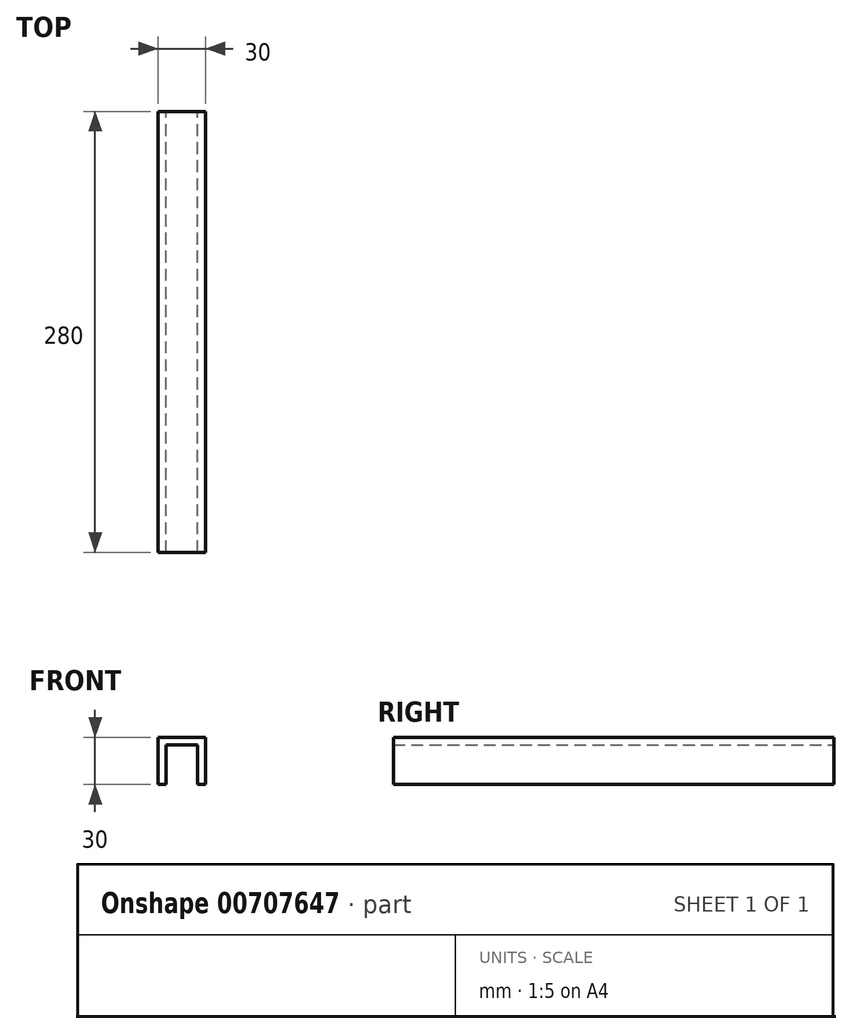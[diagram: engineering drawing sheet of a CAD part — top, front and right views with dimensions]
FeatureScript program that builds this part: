
annotation { "Feature Type Name" : "Feature", "Feature Type Description" : "" }
export const myFeature = defineFeature(function(context is Context, id is Id, definition is map)
    precondition{}
    {
        {
            var Q0;
            Q0=qCreatedBy(makeId("Front.planeOp"),FACE);
            var sketch = newSketch(context, id + "F0", { "sketchPlane" : qUnion([Q0])});
            skLineSegment(sketch, "E0.bottom", {"start": v(15, 15) * mm, "end": v(-15, 15) * mm});
            skLineSegment(sketch, "E0.top", {"start": v(15, -15) * mm, "end": v(10, -15) * mm});
            skLineSegment(sketch, "E0.left", {"start": v(15, 15) * mm, "end": v(15, -15) * mm});
            skLineSegment(sketch, "E0.right", {"start": v(-15, 15) * mm, "end": v(-15, -15) * mm});
            skPoint(sketch, "E0.middle", {"position": v(0, 0) * mm});
            skLineSegment(sketch, "E1.bottom", {"start": v(10, 10) * mm, "end": v(-10, 10) * mm});
            skLineSegment(sketch, "E1.left", {"start": v(10, 10) * mm, "end": v(10, -15) * mm});
            skLineSegment(sketch, "E1.right", {"start": v(-10, 10) * mm, "end": v(-10, -15) * mm});
            skPoint(sketch, "E1.middle", {"position": v(0, -2.5) * mm});
            skPoint(sketch, "E1.middle.positionSnap0", {"position": v(0, -15) * mm});
            skPoint(sketch, "E1.centerSnap0", {"position": v(0, -15) * mm});
            skLineSegment(sketch, "E2.trimOffspring", {"start": v(-10, -15) * mm, "end": v(-15, -15) * mm});
            skSolve(sketch);
        }
        {
            var Q0;
            Q0=makeQuery(id+"F0.imprint","IMPRINT",FACE,{"disambiguationData":[TD([[makeQuery(id+"F0.imprint","IMPRINT",EDGE,{"derivedFrom":sQuery(id+"F0.wireOp",EDGE,"E0.bottom")}),1.0]])]});
            extrude(context, id + "F1", {"entities" : qUnion([Q0]), "depth" : 140 * mm, "offsetDistance" : 25 * mm, "hasSecondDirection" : true, "secondDirectionOppositeDirection" : true, "secondDirectionDepth" : 140 * mm});
        }
    });
